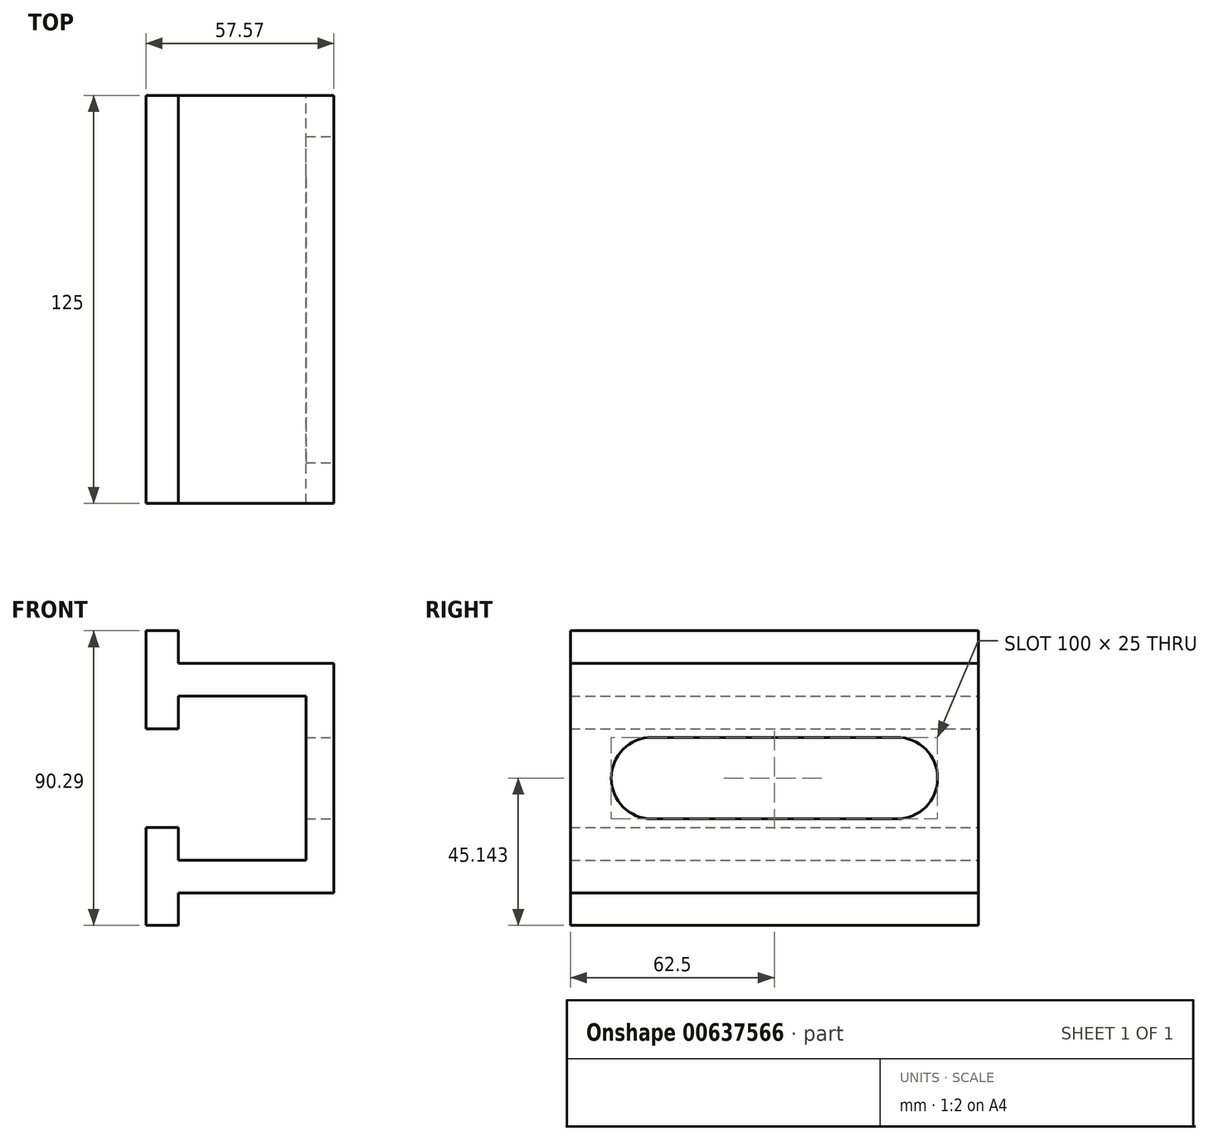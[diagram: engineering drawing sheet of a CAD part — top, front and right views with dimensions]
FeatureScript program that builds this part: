
annotation { "Feature Type Name" : "Feature", "Feature Type Description" : "" }
export const myFeature = defineFeature(function(context is Context, id is Id, definition is map)
    precondition{}
    {
        {
            var Q0;
            Q0=qCreatedBy(makeId("Front.planeOp"),FACE);
            var sketch = newSketch(context, id + "F0", { "sketchPlane" : qUnion([Q0])});
            skLineSegment(sketch, "E0", {"start": v(0, 0) * mm, "end": v(0, -10) * mm});
            skLineSegment(sketch, "E1", {"start": v(0, -10) * mm, "end": v(-10, -10) * mm});
            skLineSegment(sketch, "E2", {"start": v(-10, -10) * mm, "end": v(-10, 20) * mm});
            skLineSegment(sketch, "E3", {"start": v(-10, 20) * mm, "end": v(0, 20) * mm});
            skLineSegment(sketch, "E4", {"start": v(0, 20) * mm, "end": v(0, 10) * mm});
            skLineSegment(sketch, "E5", {"start": v(0, 10) * mm, "end": v(39, 10) * mm});
            skLineSegment(sketch, "E6", {"start": v(39, 10) * mm, "end": v(39, 60.29) * mm});
            skLineSegment(sketch, "E7", {"start": v(39, 60.29) * mm, "end": v(0, 60.29) * mm});
            skLineSegment(sketch, "E8", {"start": v(0, 60.29) * mm, "end": v(0, 50.29) * mm});
            skLineSegment(sketch, "E9", {"start": v(0, 50.29) * mm, "end": v(-10, 50.29) * mm});
            skLineSegment(sketch, "E10", {"start": v(-10, 50.29) * mm, "end": v(-10, 80.29) * mm});
            skLineSegment(sketch, "E11", {"start": v(-10, 80.29) * mm, "end": v(0, 80.29) * mm});
            skLineSegment(sketch, "E12", {"start": v(0, 80.29) * mm, "end": v(0, 70.29) * mm});
            skLineSegment(sketch, "E13", {"start": v(0, 70.29) * mm, "end": v(47.57, 70.29) * mm});
            skLineSegment(sketch, "E14", {"start": v(47.57, 70.29) * mm, "end": v(47.57, 0) * mm});
            skLineSegment(sketch, "E15", {"start": v(47.57, 0) * mm, "end": v(0, 0) * mm});
            skSolve(sketch);
        }
        {
            var Q0;
            Q0 = qSketchRegion(id + "F0", true);
            extrude(context, id + "F1", {"entities" : qUnion([Q0]), "depth" : 125 * mm, "offsetDistance" : 25 * mm});
        }
        {
            var Q0;
            Q0=makeQuery(id+"F1.opExtrude","SWEPT_FACE",FACE,{"disambiguationData":[OSD([sQuery(id+"F0.wireOp",EDGE,"E14")])]});
            var sketch = newSketch(context, id + "F2", { "sketchPlane" : qUnion([Q0])});
            skArc(sketch, "E16", {"start": v(-100, 47.64) * mm, "mid": v(-112.5, 35.14) * mm, "end": v(-100, 22.64) * mm});
            skPoint(sketch, "E16.centerSnap0", {"position": v(-125, 35.14) * mm});
            skArc(sketch, "E17", {"start": v(-25, 22.64) * mm, "mid": v(-12.5, 35.14) * mm, "end": v(-25, 47.64) * mm});
            skPoint(sketch, "E17.centerSnap0", {"position": v(0, 35.14) * mm});
            skLineSegment(sketch, "E18", {"start": v(-100, 47.64) * mm, "end": v(-25, 47.64) * mm});
            skLineSegment(sketch, "E19", {"start": v(-25, 22.64) * mm, "end": v(-100, 22.64) * mm});
            skSolve(sketch);
        }
        {
            var Q0;
            Q0 = qSketchRegion(id + "F2", true);
            extrude(context, id + "F3", {"entities" : qUnion([Q0]), "operationType" : NewBodyOperationType.REMOVE, "oppositeDirection" : true, "depth" : 25 * mm, "offsetDistance" : 25 * mm});
        }
    });
